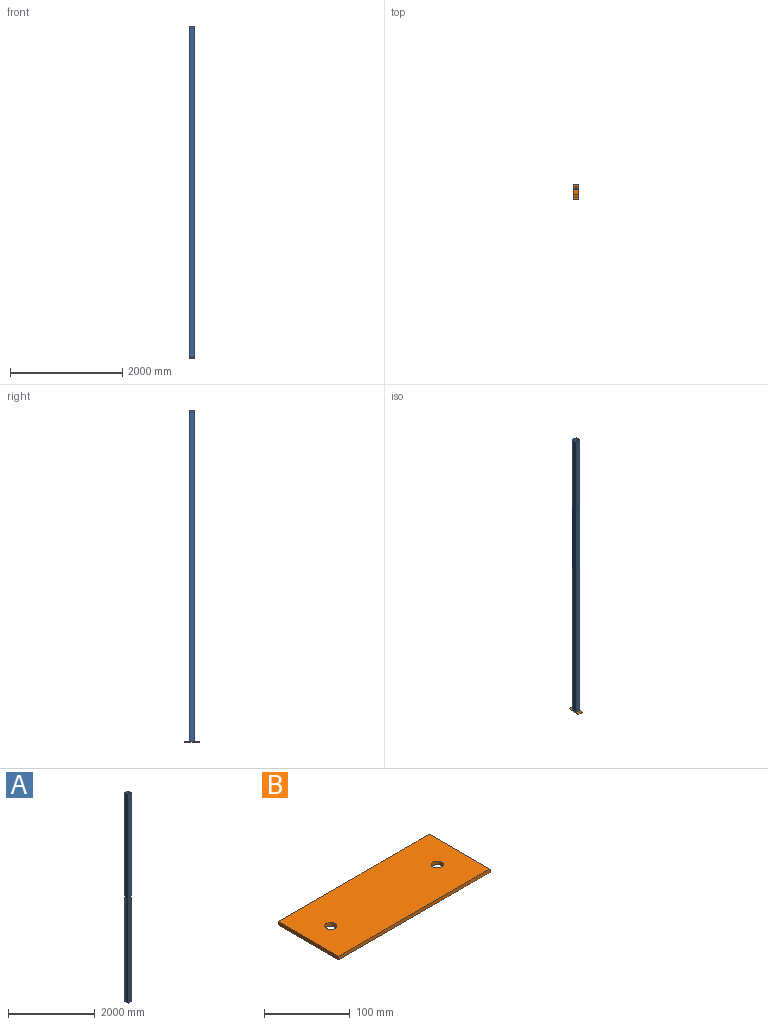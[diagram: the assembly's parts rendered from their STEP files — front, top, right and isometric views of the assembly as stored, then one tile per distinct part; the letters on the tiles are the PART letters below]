
ASSEMBLY  parts=2 mates=1
PART A: 10 faces, bbox 100x100x5900 mm
  f0: plane 5900x100mm, normal (1,0,0), area 590000mm2, adj f1,f7,f8,f9
  f1: plane 5900x100mm, normal (0,1,0), area 590000mm2, adj f0,f2,f8,f9
  f2: plane 5900x100mm, normal (-1,0,0), area 590000mm2, adj f1,f7,f8,f9
  f3: plane 5900x94mm, normal (0,-1,0), area 554600mm2, adj f4,f6,f8,f9
  f4: plane 5900x94mm, normal (-1,0,0), area 554600mm2, adj f3,f5,f8,f9
  f5: plane 5900x94mm, normal (0,1,0), area 554600mm2, adj f4,f6,f8,f9
  f6: plane 5900x94mm, normal (1,0,0), area 554600mm2, adj f3,f5,f8,f9
  f7: plane 5900x100mm, normal (0,-1,0), area 590000mm2, adj f0,f2,f8,f9
  f8: plane 100x100mm, normal (0,0,1), area 1164mm2, adj f0,f1,f2,f3,f4,f5,f6,f7
  f9: plane 100x100mm, normal (0,0,-1), area 1164mm2, adj f0,f1,f2,f3,f4,f5,f6,f7
PART B: 8 faces, bbox 250x100x5 mm
  f0: plane 100x5mm, normal (1,0,0), area 500mm2, adj f1,f5,f6,f7
  f1: plane 250x5mm, normal (0,1,0), area 1250mm2, adj f0,f2,f6,f7
  f2: plane 100x5mm, normal (-1,0,0), area 500mm2, adj f1,f5,f6,f7
  f3: cylinder r=7mm len=14mm, axis (0,0,-1), area 219.9mm2, adj f6,f7
  f4: cylinder r=7mm len=14mm, axis (0,0,-1), area 219.9mm2, adj f6,f7
  f5: plane 250x5mm, normal (0,-1,0), area 1250mm2, adj f0,f2,f6,f7
  f6: plane 250x100mm, normal (0,0,1), area 24692.1mm2, adj f0,f1,f2,f3,f4,f5
  f7: plane 250x100mm, normal (0,0,-1), area 24692.1mm2, adj f0,f1,f2,f3,f4,f5
PLACE A t=(-71.13,-47.07,-2959.01)mm
PLACE B rot(axis=(0,0,-1),90deg) t=(-71.13,-47.07,-2964.01)mm
MATE fastened B.f6 <-> A.f9  axis (0,0,1) through (-121.13,77.93,-2959.01)mm
